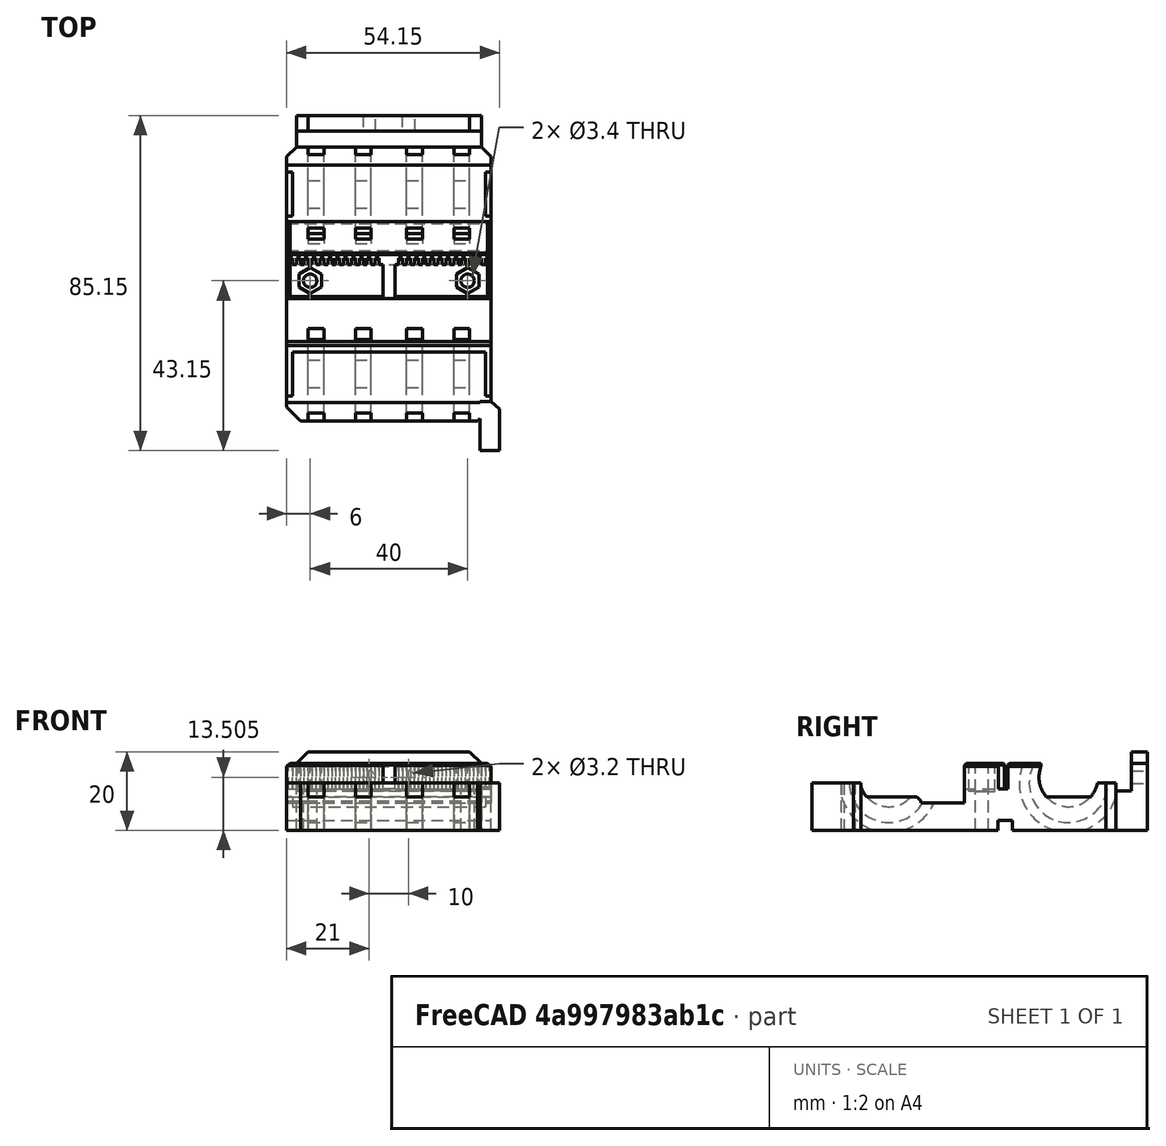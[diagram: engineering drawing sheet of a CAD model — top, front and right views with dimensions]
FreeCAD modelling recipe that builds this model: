
FCSTD DOCUMENT  (FreeCAD 0.19R)
Label: x-carriage
License: All rights reserved
LicenseURL: http://en.wikipedia.org/wiki/All_rights_reserved
objects: Part::Box×56, Part::Cylinder×16, Part::Fuse×12, Part::Cut×7, Part::MultiFuse×6, Sketcher::SketchObject×4, PartDesign::Pad×3, Part::Prism×2, PartDesign::FeatureBase×1, PartDesign::Chamfer×1, PartDesign::Pocket×1, PartDesign::Body×1
note: 115 computed .brp shape members not serialized (recipe doc carries the construction recipe); baked Part::Feature solids carry a one-line shape summary decoded from their .brp

FEATURE [Part::Box] cube
  AttacherType = Attacher::AttachEngine3D
  Height = 12
  Length = 24
  Placement = pos=(26,-12.65,0) rot=(0,0,1;1.5708rad)
  Width = 52
FEATURE [Part::Box] cube001
  AttacherType = Attacher::AttachEngine3D
  Height = 12
  Length = 24
  Placement = pos=(26,33,0) rot=(0,0,1;1.5708rad)
  Width = 52
FEATURE [Part::Box] cube002
  AttacherType = Attacher::AttachEngine3D
  Height = 17
  Length = 52
  Placement = pos=(-26,17,0) rot=(0,0,1;0rad)
  Width = 21
FEATURE [Part::Box] cube003
  AttacherType = Attacher::AttachEngine3D
  Height = 8.5
  Length = 52
  Placement = pos=(-26,-12,0) rot=(0,0,1;0rad)
  Width = 69
FEATURE [Part::MultiFuse] Group
  Shapes = -> [cube,cube001,cube002,cube003]
FEATURE [Part::Box] cube004
  AttacherType = Attacher::AttachEngine3D
  Height = 15
  Length = 3
  Placement = pos=(-1.5,13,10.5) rot=(0,0,1;0rad)
  Width = 16
FEATURE [Part::Box] cube005
  AttacherType = Attacher::AttachEngine3D
  Height = 15
  Length = 70
  Placement = pos=(-35,7.5,7) rot=(0,0,1;0rad)
  Width = 11
FEATURE [Part::Box] cube006
  AttacherType = Attacher::AttachEngine3D
  Height = 15
  Length = 70
  Placement = pos=(-35,0,8.5) rot=(0,0,1;0rad)
  Width = 11
FEATURE [Part::Box] cube007
  AttacherType = Attacher::AttachEngine3D
  Height = 15
  Length = 70
  Placement = pos=(-35,8,7) rot=(1,0,0;0.785398rad)
  Width = 11
FEATURE [Part::Box] cube008
  AttacherType = Attacher::AttachEngine3D
  Height = 15
  Length = 60
  Placement = pos=(-30,28.75,10.5) rot=(0,0,1;0rad)
  Width = 0.9
FEATURE [Part::Box] cube009
  AttacherType = Attacher::AttachEngine3D
  Height = 15
  Length = 68
  Placement = pos=(-34,29.25,16.2) rot=(1,0,0;0.785398rad)
  Width = 15
FEATURE [Part::Box] cube010 .. cube043  x34 (patterned run collapsed; names and placements below)
  AttacherType = Attacher::AttachEngine3D
  Height = 15
  Length = 1
  Width = 1.7
  placements: 34 in arithmetic series — first pos=(33.5,27.15,10.5) rot=(0,0,1;0rad), step (-2,0,0), last pos=(-32.5,27.15,10.5) rot=(0,0,1;0rad)
FEATURE [Part::MultiFuse] Group001
  Shapes = -> [cube010,cube011,cube012,cube013,cube014,cube015,cube016,cube017,cube018,cube019,cube020,cube021,cube022,cube023,cube024,cube025,cube026,cube027,cube028,cube029,cube030,cube031,cube032,cube033,cube034,cube035,cube036,cube037,cube038,cube039,cube040,cube041,cube042,cube043]
FEATURE [Part::MultiFuse] Group002
  Shapes = -> [cube004,cube005,cube006,cube007,cube008,cube009,Group001]
FEATURE [Part::Cylinder] cylinder
  Angle = 360
  AttacherType = Attacher::AttachEngine3D
  Height = 60
  Placement = pos=(0,30,13.5) rot=(1,0,0;1.5708rad)
  Radius = 7.5
FEATURE [Part::Box] cube044
  AttacherType = Attacher::AttachEngine3D
  Height = 8
  Length = 24
  Placement = pos=(-12,-30.5,0.5) rot=(0,0,1;0rad)
  Width = 6
FEATURE [Part::Box] cube045
  AttacherType = Attacher::AttachEngine3D
  Height = 8
  Length = 24
  Placement = pos=(-12,24.5,0.5) rot=(0,0,1;0rad)
  Width = 6
FEATURE [Part::Fuse] union
  Base = -> cube044
  Tool = -> cube045
FEATURE [Part::Cut] difference
  Base = -> cylinder
  Tool = -> union
FEATURE [Part::Cylinder] cylinder001
  Angle = 360
  AttacherType = Attacher::AttachEngine3D
  Height = 4
  Placement = pos=(0,-4,12) rot=(1,0,0;1.5708rad)
  Radius = 12.5
FEATURE [Part::Cylinder] cylinder002
  Angle = 360
  AttacherType = Attacher::AttachEngine3D
  Height = 4
  Placement = pos=(0,8,12) rot=(1,0,0;1.5708rad)
  Radius = 12.5
FEATURE [Part::Fuse] union001
  Base = -> cylinder001
  Tool = -> cylinder002
FEATURE [Part::Cylinder] cylinder003
  Angle = 360
  AttacherType = Attacher::AttachEngine3D
  Height = 24
  Placement = pos=(0,10,12) rot=(1,0,0;1.5708rad)
  Radius = 10
FEATURE [Part::Cut] difference001
  Base = -> union001
  Placement = pos=(0,-12.5,0) rot=(0,0,1;0rad)
  Tool = -> cylinder003
FEATURE [Part::Cylinder] cylinder004
  Angle = 360
  AttacherType = Attacher::AttachEngine3D
  Height = 4
  Placement = pos=(0,-4,12) rot=(1,0,0;1.5708rad)
  Radius = 12.5
FEATURE [Part::Cylinder] cylinder005
  Angle = 360
  AttacherType = Attacher::AttachEngine3D
  Height = 4
  Placement = pos=(0,8,12) rot=(1,0,0;1.5708rad)
  Radius = 12.5
FEATURE [Part::Fuse] union002
  Base = -> cylinder004
  Tool = -> cylinder005
FEATURE [Part::Cylinder] cylinder006
  Angle = 360
  AttacherType = Attacher::AttachEngine3D
  Height = 24
  Placement = pos=(0,10,12) rot=(1,0,0;1.5708rad)
  Radius = 10
FEATURE [Part::Cut] difference002
  Base = -> union002
  Placement = pos=(0,12.5,0) rot=(0,0,1;0rad)
  Tool = -> cylinder006
FEATURE [Part::Fuse] Group003
  Base = -> difference001
  Tool = -> difference002
FEATURE [Part::Fuse] Group004
  Base = -> difference
  Placement = pos=(0,-0.65,0) rot=(0,0,1;1.5708rad)
  Tool = -> Group003
FEATURE [Part::Cylinder] cylinder007
  Angle = 360
  AttacherType = Attacher::AttachEngine3D
  Height = 60
  Placement = pos=(0,30,13.5) rot=(1,0,0;1.5708rad)
  Radius = 7.5
FEATURE [Part::Box] cube046
  AttacherType = Attacher::AttachEngine3D
  Height = 8
  Length = 24
  Placement = pos=(-12,-30.5,0.5) rot=(0,0,1;0rad)
  Width = 6
FEATURE [Part::Box] cube047
  AttacherType = Attacher::AttachEngine3D
  Height = 8
  Length = 24
  Placement = pos=(-12,24.5,0.5) rot=(0,0,1;0rad)
  Width = 6
FEATURE [Part::Fuse] union003
  Base = -> cube046
  Tool = -> cube047
FEATURE [Part::Cut] difference003
  Base = -> cylinder007
  Tool = -> union003
FEATURE [Part::Cylinder] cylinder008
  Angle = 360
  AttacherType = Attacher::AttachEngine3D
  Height = 4
  Placement = pos=(0,-4,12) rot=(1,0,0;1.5708rad)
  Radius = 12.5
FEATURE [Part::Cylinder] cylinder009
  Angle = 360
  AttacherType = Attacher::AttachEngine3D
  Height = 4
  Placement = pos=(0,8,12) rot=(1,0,0;1.5708rad)
  Radius = 12.5
FEATURE [Part::Fuse] union004
  Base = -> cylinder008
  Tool = -> cylinder009
FEATURE [Part::Cylinder] cylinder010
  Angle = 360
  AttacherType = Attacher::AttachEngine3D
  Height = 24
  Placement = pos=(0,10,12) rot=(1,0,0;1.5708rad)
  Radius = 10
FEATURE [Part::Cut] difference004
  Base = -> union004
  Placement = pos=(0,-12.5,0) rot=(0,0,1;0rad)
  Tool = -> cylinder010
FEATURE [Part::Cylinder] cylinder011
  Angle = 360
  AttacherType = Attacher::AttachEngine3D
  Height = 4
  Placement = pos=(0,-4,12) rot=(1,0,0;1.5708rad)
  Radius = 12.5
FEATURE [Part::Cylinder] cylinder012
  Angle = 360
  AttacherType = Attacher::AttachEngine3D
  Height = 4
  Placement = pos=(0,8,12) rot=(1,0,0;1.5708rad)
  Radius = 12.5
FEATURE [Part::Fuse] union005
  Base = -> cylinder011
  Tool = -> cylinder012
FEATURE [Part::Cylinder] cylinder013
  Angle = 360
  AttacherType = Attacher::AttachEngine3D
  Height = 24
  Placement = pos=(0,10,12) rot=(1,0,0;1.5708rad)
  Radius = 10
FEATURE [Part::Cut] difference005
  Base = -> union005
  Placement = pos=(0,12.5,0) rot=(0,0,1;0rad)
  Tool = -> cylinder013
FEATURE [Part::Fuse] Group005
  Base = -> difference004
  Tool = -> difference005
FEATURE [Part::Fuse] Group006
  Base = -> difference003
  Placement = pos=(0,45,0) rot=(0,0,1;1.5708rad)
  Tool = -> Group005
FEATURE [Part::Box] cube048
  AttacherType = Attacher::AttachEngine3D
  Height = 2.6
  Length = 80
  Placement = pos=(-40,27,-0.1) rot=(0,0,1;0rad)
  Width = 3.7
FEATURE [Part::Cylinder] cylinder014
  Angle = 360
  AttacherType = Attacher::AttachEngine3D
  Height = 20
  Placement = pos=(20,0,0) rot=(0,0,1;0rad)
  Radius = 1.7
FEATURE [Part::Prism] prism
  AttacherType = Attacher::AttachEngine3D
  Circumradius = 3.3
  FirstAngle = 0
  Height = 20
  Placement = pos=(20,0,10) rot=(0,0,1;0.523599rad)
  Polygon = 6
  SecondAngle = 0
FEATURE [Part::Fuse] Matrix_Union
  Base = -> cylinder014
  Placement = pos=(0,23,-0.1) rot=(0,0,1;0rad)
  Tool = -> prism
FEATURE [Part::Cylinder] cylinder015
  Angle = 360
  AttacherType = Attacher::AttachEngine3D
  Height = 20
  Placement = pos=(-20,0,0) rot=(0,0,1;0rad)
  Radius = 1.7
FEATURE [Part::Prism] prism001
  AttacherType = Attacher::AttachEngine3D
  Circumradius = 3.3
  FirstAngle = 0
  Height = 20
  Placement = pos=(-20,0,10) rot=(0,0,1;0.523599rad)
  Polygon = 6
  SecondAngle = 0
FEATURE [Part::Fuse] Matrix_Union001
  Base = -> cylinder015
  Placement = pos=(0,23,-0.1) rot=(0,0,1;0rad)
  Tool = -> prism001
FEATURE [Part::MultiFuse] Group007
  Shapes = -> [Group004,Group006,cube048,Matrix_Union,Matrix_Union001]
FEATURE [Part::Box] cube049
  AttacherType = Attacher::AttachEngine3D
  Height = 20
  Length = 30
  Placement = pos=(26,54.5,-0.1) rot=(0,0,1;0.785398rad)
  Width = 30
FEATURE [Part::Box] cube050
  AttacherType = Attacher::AttachEngine3D
  Height = 20
  Length = 30
  Placement = pos=(-26,54.5,-0.1) rot=(0,0,1;0.785398rad)
  Width = 30
FEATURE [Part::Box] cube051
  AttacherType = Attacher::AttachEngine3D
  Height = 20
  Length = 30
  Placement = pos=(26,-9.15,-0.1) rot=(0,0,1;3.92699rad)
  Width = 30
FEATURE [Part::Box] cube052
  AttacherType = Attacher::AttachEngine3D
  Height = 20
  Length = 30
  Placement = pos=(-26,-9.15,-0.1) rot=(0,0,1;3.92699rad)
  Width = 30
FEATURE [Part::Box] cube053
  AttacherType = Attacher::AttachEngine3D
  Height = 10
  Length = 52
  Placement = pos=(-26,17,15) rot=(1,0,0;0.785398rad)
  Width = 10
FEATURE [Part::Box] cube054
  AttacherType = Attacher::AttachEngine3D
  Height = 10
  Length = 10
  Placement = pos=(-27.5,17,15) rot=(0,-1,0;0.698132rad)
  Width = 40
FEATURE [Part::Box] cube055
  AttacherType = Attacher::AttachEngine3D
  Height = 10
  Length = 10
  Placement = pos=(27.5,17,15) rot=(0,-1,0;0.872665rad)
  Width = 40
FEATURE [Part::MultiFuse] Group008
  Shapes = -> [cube049,cube050,cube051,cube052,cube053,cube054,cube055]
FEATURE [Part::MultiFuse] union006
  Shapes = -> [Group002,Group007,Group008]
FEATURE [Part::Cut] difference006
  Base = -> Group
  Tool = -> union006
FEATURE [PartDesign::FeatureBase] BaseFeature
  BaseFeature = -> difference006
FEATURE [Sketcher::SketchObject] Sketch
  ExternalGeometry = -> [BaseFeature]
  MapMode = 5
  Placement = pos=(0,0,0) rot=(1,0,0;3.14159rad)
  Support = -> [BaseFeature]
  sketch-geometry (6):
    g0: LineSegment StartX=26 StartY=7.72233 StartZ=0 EndX=28.15 EndY=9.65165 EndZ=0
    g1: LineSegment StartX=28.15 StartY=9.65165 StartZ=0 EndX=28.15 EndY=20.15 EndZ=0
    g2: LineSegment StartX=28.15 StartY=20.15 StartZ=0 EndX=23.15 EndY=20.15 EndZ=0
    g3: LineSegment StartX=23.15 StartY=20.15 StartZ=0 EndX=23.15 EndY=12 EndZ=0
    g4: LineSegment StartX=23.15 StartY=12 StartZ=0 EndX=23.15 EndY=7.72233 EndZ=0
    g5: LineSegment StartX=23.15 StartY=7.72233 StartZ=0 EndX=26 EndY=7.72233 EndZ=0
  constraints (15):
    c: PointOnObject(g0,g-4)
    c: Coincident(g0,g1)
    c: Vertical(g1)
    c: Coincident(g1,g2)
    c: Horizontal(g2)
    c: Coincident(g2,g3)
    c: Coincident(g3,g-5)
    c: Coincident(g3,g4)
    c: Vertical(g4)
    c: Coincident(g4,g5)
    c: Coincident(g5,g0)
    c: Horizontal(g5)
    c: Vertical(g3)
    c: Distance(g2,g-6) = 7.5
    c: DistanceX(g2,g2) = 5
FEATURE [PartDesign::Pad] Pad
  BaseFeature = -> BaseFeature
  Direction = (1,1,1)
  Length = 12
  Length2 = 100
  Profile = -> Sketch
  Refine = true
  Reversed = true
  Type = 0
FEATURE [Sketcher::SketchObject] Sketch001
  ExternalGeometry = -> [Pad]
  MapMode = 5
  Placement = pos=(0,0,0) rot=(1,0,0;3.14159rad)
  Support = -> [Pad]
  sketch-geometry (4):
    g0: LineSegment StartX=-23.5 StartY=-57 StartZ=0 EndX=23.5 EndY=-57 EndZ=0
    g1: LineSegment StartX=23.5 StartY=-57 StartZ=0 EndX=23.5 EndY=-65 EndZ=0
    g2: LineSegment StartX=23.5 StartY=-65 StartZ=0 EndX=-23.5 EndY=-65 EndZ=0
    g3: LineSegment StartX=-23.5 StartY=-65 StartZ=0 EndX=-23.5 EndY=-57 EndZ=0
  constraints (10):
    c: Coincident(g0,g1)
    c: Coincident(g1,g2)
    c: Coincident(g2,g3)
    c: Coincident(g3,g0)
    c: Horizontal(g2)
    c: Vertical(g1)
    c: Vertical(g3)
    c: Coincident(g0,g-3)
    c: Coincident(g0,g-3)
    c: DistanceY(g3,g3) = 8
FEATURE [PartDesign::Pad] Pad001
  BaseFeature = -> Pad
  Direction = (1,1,1)
  Length = 10
  Length2 = 100
  Profile = -> Sketch001
  Reversed = true
  Type = 0
FEATURE [Sketcher::SketchObject] Sketch002
  ExternalGeometry = -> [Pad001]
  MapMode = 5
  Placement = pos=(0,0,10) rot=(0,0,1;0rad)
  Support = -> [Pad001]
  sketch-geometry (4):
    g0: LineSegment StartX=-23.5 StartY=65 StartZ=0 EndX=23.5 EndY=65 EndZ=0
    g1: LineSegment StartX=23.5 StartY=65 StartZ=0 EndX=23.5 EndY=61 EndZ=0
    g2: LineSegment StartX=23.5 StartY=61 StartZ=0 EndX=-23.5 EndY=61 EndZ=0
    g3: LineSegment StartX=-23.5 StartY=61 StartZ=0 EndX=-23.5 EndY=65 EndZ=0
  constraints (11):
    c: Coincident(g0,g1)
    c: Coincident(g1,g2)
    c: Coincident(g2,g3)
    c: Coincident(g3,g0)
    c: Horizontal(g0)
    c: Horizontal(g2)
    c: Vertical(g1)
    c: Vertical(g3)
    c: Coincident(g0,g-4)
    c: PointOnObject(g1,g-5)
    c: DistanceY(g1,g1) = 4
FEATURE [PartDesign::Pad] Pad002
  BaseFeature = -> Pad001
  Direction = (1,1,1)
  Length = 10
  Length2 = 100
  Profile = -> Sketch002
  Type = 0
FEATURE [PartDesign::Chamfer] Chamfer
  Angle = 45
  Base = -> Pad002 [Edge747,Edge750]
  BaseFeature = -> Pad002
  ChamferType = 0
  FlipDirection = false
  Size = 3
  Size2 = 1
  SupportTransform = false
FEATURE [Sketcher::SketchObject] Sketch003
  MapMode = 5
  Placement = pos=(0,65,0) rot=(0,0.707107,0.707107;3.14159rad)
  Support = -> [Chamfer]
  sketch-geometry (2):
    g0: Circle CenterX=-5 CenterY=13.5048 CenterZ=0 NormalX=0 NormalY=0 NormalZ=1 AngleXU=0 Radius=1.6
    g1: Circle CenterX=5 CenterY=13.5048 CenterZ=0 NormalX=0 NormalY=0 NormalZ=1 AngleXU=0 Radius=1.6
  constraints (4):
    c: Symmetric(g1,g0,g-2)
    c: Radius(g0) = 1.6
    c: Equal(g0,g1)
    c: Distance(g0,g1) = 10
FEATURE [PartDesign::Pocket] Pocket
  BaseFeature = -> Chamfer
  Length = 5
  Length2 = 100
  Profile = -> Sketch003
  Refine = true
  Type = 0
FEATURE [PartDesign::Body] Body
  BaseFeature = -> difference006
  Group = -> [BaseFeature,Sketch,Pad,Sketch001,Pad001,Sketch002,Pad002,Chamfer,Sketch003,Pocket]
  Origin = -> Origin
  Tip = -> Pocket
